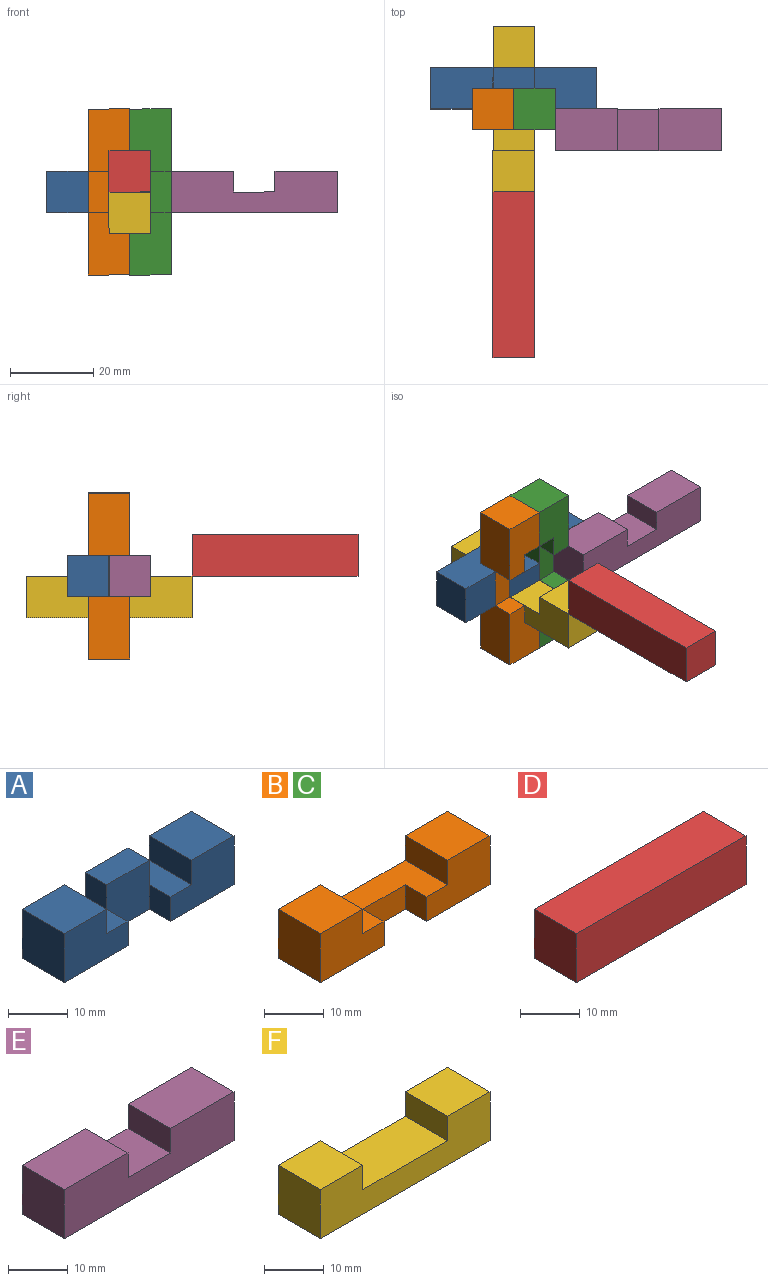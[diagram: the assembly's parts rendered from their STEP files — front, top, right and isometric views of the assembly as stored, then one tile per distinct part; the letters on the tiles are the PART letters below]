
ASSEMBLY  parts=6 mates=5
PART A: 18 faces, bbox 40x10x10 mm
  f0: plane 10x5mm, normal (0,0,1), area 50mm2, adj f1,f5,f11,f12,f16
  f1: plane 15x10mm, normal (0,-1,0), area 125mm2, adj f0,f2,f4,f7,f11,f12
  f2: plane 40x10mm, normal (0,0,-1), area 350mm2, adj f1,f3,f5,f6,f7,f12,f13,f14
  f3: plane 15x10mm, normal (0,-1,0), area 125mm2, adj f2,f6,f8,f9,f10,f13
  f4: plane 10x10mm, normal (0,0,1), area 100mm2, adj f1,f5,f7,f11
  f5: plane 40x10mm, normal (0,1,0), area 350mm2, adj f0,f2,f4,f6,f7,f8,f9,f10
  f6: plane 10x10mm, normal (-1,0,0), area 100mm2, adj f2,f3,f5,f8
  f7: plane 10x10mm, normal (1,0,0), area 100mm2, adj f1,f2,f4,f5
  f8: plane 10x10mm, normal (0,0,1), area 100mm2, adj f3,f5,f6,f9
  f9: plane 10x5mm, normal (1,0,0), area 50mm2, adj f3,f5,f8,f10
  f10: plane 10x5mm, normal (0,0,1), area 50mm2, adj f3,f5,f9,f13,f15
  f11: plane 10x5mm, normal (-1,0,0), area 50mm2, adj f0,f1,f4,f5
  f12: plane 5x5mm, normal (-1,0,0), area 25mm2, adj f0,f1,f2,f14
  f13: plane 5x5mm, normal (1,0,0), area 25mm2, adj f2,f3,f10,f14
  f14: plane 10x10mm, normal (0,-1,0), area 100mm2, adj f2,f12,f13,f15,f16,f17
  f15: plane 5x5mm, normal (-1,0,0), area 25mm2, adj f5,f10,f14,f17
  f16: plane 5x5mm, normal (1,0,0), area 25mm2, adj f0,f5,f14,f17
  f17: plane 10x5mm, normal (0,0,1), area 50mm2, adj f5,f14,f15,f16
PART B: 14 faces, bbox 40x10x10 mm
  f0: plane 15x10mm, normal (0,-1,0), area 125mm2, adj f1,f3,f6,f9,f10,f11
  f1: plane 40x10mm, normal (0,0,-1), area 350mm2, adj f0,f2,f4,f5,f6,f11,f12,f13
  f2: plane 15x10mm, normal (0,-1,0), area 125mm2, adj f1,f5,f7,f8,f9,f12
  f3: plane 10x10mm, normal (0,0,1), area 100mm2, adj f0,f4,f6,f10
  f4: plane 40x10mm, normal (0,1,0), area 300mm2, adj f1,f3,f5,f6,f7,f8,f9,f10
  f5: plane 10x10mm, normal (-1,0,0), area 100mm2, adj f1,f2,f4,f7
  f6: plane 10x10mm, normal (1,0,0), area 100mm2, adj f0,f1,f3,f4
  f7: plane 10x10mm, normal (0,0,1), area 100mm2, adj f2,f4,f5,f8
  f8: plane 10x5mm, normal (1,0,0), area 50mm2, adj f2,f4,f7,f9
  f9: plane 20x10mm, normal (0,0,1), area 150mm2, adj f0,f2,f4,f8,f10,f11,f12,f13
  f10: plane 10x5mm, normal (-1,0,0), area 50mm2, adj f0,f3,f4,f9
  f11: plane 5x5mm, normal (-1,0,0), area 25mm2, adj f0,f1,f9,f13
  f12: plane 5x5mm, normal (1,0,0), area 25mm2, adj f1,f2,f9,f13
  f13: plane 10x5mm, normal (0,-1,0), area 50mm2, adj f1,f9,f11,f12
PART C: same geometry as B
PART D: 6 faces, bbox 40x10x10 mm
  f0: plane 40x10mm, normal (0,1,0), area 400mm2, adj f1,f3,f4,f5
  f1: plane 10x10mm, normal (-1,0,0), area 100mm2, adj f0,f2,f4,f5
  f2: plane 40x10mm, normal (0,-1,0), area 400mm2, adj f1,f3,f4,f5
  f3: plane 10x10mm, normal (1,0,0), area 100mm2, adj f0,f2,f4,f5
  f4: plane 40x10mm, normal (0,0,1), area 400mm2, adj f0,f1,f2,f3
  f5: plane 40x10mm, normal (0,0,-1), area 400mm2, adj f0,f1,f2,f3
PART E: 10 faces, bbox 40x10x10 mm
  f0: plane 40x10mm, normal (0,-1,0), area 350mm2, adj f1,f3,f4,f5,f6,f7,f8,f9
  f1: plane 15x10mm, normal (0,0,1), area 150mm2, adj f0,f2,f4,f9
  f2: plane 40x10mm, normal (0,1,0), area 350mm2, adj f1,f3,f4,f5,f6,f7,f8,f9
  f3: plane 10x10mm, normal (-1,0,0), area 100mm2, adj f0,f2,f5,f6
  f4: plane 10x10mm, normal (1,0,0), area 100mm2, adj f0,f1,f2,f6
  f5: plane 15x10mm, normal (0,0,1), area 150mm2, adj f0,f2,f3,f7
  f6: plane 40x10mm, normal (0,0,-1), area 400mm2, adj f0,f2,f3,f4
  f7: plane 10x5mm, normal (1,0,0), area 50mm2, adj f0,f2,f5,f8
  f8: plane 10x10mm, normal (0,0,1), area 100mm2, adj f0,f2,f7,f9
  f9: plane 10x5mm, normal (-1,0,0), area 50mm2, adj f0,f1,f2,f8
PART F: 10 faces, bbox 40x10x10 mm
  f0: plane 40x10mm, normal (0,-1,0), area 300mm2, adj f1,f3,f4,f5,f6,f7,f8,f9
  f1: plane 10x10mm, normal (0,0,1), area 100mm2, adj f0,f2,f4,f9
  f2: plane 40x10mm, normal (0,1,0), area 300mm2, adj f1,f3,f4,f5,f6,f7,f8,f9
  f3: plane 10x10mm, normal (-1,0,0), area 100mm2, adj f0,f2,f5,f6
  f4: plane 10x10mm, normal (1,0,0), area 100mm2, adj f0,f1,f2,f6
  f5: plane 10x10mm, normal (0,0,1), area 100mm2, adj f0,f2,f3,f7
  f6: plane 40x10mm, normal (0,0,-1), area 400mm2, adj f0,f2,f3,f4
  f7: plane 10x5mm, normal (1,0,0), area 50mm2, adj f0,f2,f5,f8
  f8: plane 20x10mm, normal (0,0,1), area 200mm2, adj f0,f2,f7,f9
  f9: plane 10x5mm, normal (-1,0,0), area 50mm2, adj f0,f1,f2,f8
PLACE A rot(axis=(0,0.71,-0.71),180deg) t=(-5,30,-10)mm
PLACE B rot(axis=(0,1,0),90deg) t=(-15,20,-10)mm fixed
PLACE C rot(axis=(0,-1,0),90deg) t=(5,20,-10)mm
PLACE D rot(axis=(0.58,0.58,0.58),120deg) t=(-10,-20,-5)mm
PLACE E t=(25,15,-15)mm
PLACE F rot(axis=(0,0,1),90deg) t=(-5,20,-20)mm
MATE slider D.f3 <-> F.f3  axis (0,1,0) through (-5,0,-10)mm
MATE slider B.f4 <-> F.f3  axis (0,1,0) through (-5,25,-20)mm
MATE fastened B.f7 <-> C.f3  axis (1,0,0) through (-5,20,5)mm
MATE fastened A.f2 <-> F.f9  axis (0,1,0) through (-5,30,-10)mm
MATE slider E.f3 <-> C.f1  axis (-1,0,0) through (5,20,-10)mm
